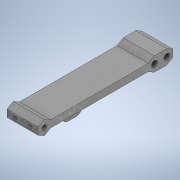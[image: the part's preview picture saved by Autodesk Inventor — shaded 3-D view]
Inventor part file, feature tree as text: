
AUTODESK INVENTOR PART (.ipt)
format: ipt  version: 2020 (Build 240168000, 168)  size: 425,984 bytes
history: native  units: in
note: dims shown in document units (in); Inventor stores cm internally (conversion verified against a paired STEP export)
features: extrude x5, sketch x5, plane x3, projected_geometry x3, mirror x1, fillet x1
ambient origin geometry x8: Origin, YZ Plane, XZ Plane, XY Plane, X Axis, Y Axis, Z Axis, Center Point
bodies: Solid1 (feature_tree)
feature tree (18):
  extrude  "Extrusion1"  Depth=3.4256in
  plane  "Work Plane1"
  extrude  "Extrusion4"  Depth=0.7874in
  plane  "Work Plane2"
  extrude  "Extrusion6"  Depth=3.1106in
  mirror  "Mirror2"
  extrude  "Extrusion8"  Depth=0.315in
  fillet  "Fillet1"  Radius=0.1476in
  sketch  "Sketch11"  dims[d34=0.2362in d35=0.0in d38=0.315in d39=0.2756in d40=-0.3092in d60=1.0994in d61=0.1378in d63=1.1811in d64=0.1575in d65=0.0in d66=0.126in d67=0.1575in d69=0.1949in d70=0.0906in d71=0.3937in d72=0.3937in d73=0.0in]
  plane  "Work Plane3"
  extrude  "Extrusion9"  TaperAngle=0.0deg  [1 undecoded]
  sketch  "Sketch1"  dims[d0=0.1818in d1=3.4256in]
  sketch  "Sketch5"  dims[d2=0.122in d3=0.7874in]
  sketch  "Sketch7"  dims[d4=0.0in d28=3.1106in]
  projected_geometry  "Projected Loop7"
  projected_geometry  "Projected Loop8"
  sketch  "Sketch10"  dims[d29=0.315in d31=0.315in d33=0.1476in]
  projected_geometry  "Projected Loop10"
note: 1 required parameter value undecoded (feature->parameter linkage not recoverable at this tier; creation-order binding heuristic only, values carry confidence <= 0.55)
